# Revit family: WALL WASHER FOCUS RGBW_LVL4030RGB.10
name_source: partatom
category: Luminarias
units: mm (PartAtom-declared; Revit-internal decimal feet)

## family parameters
Compartido = No
Corte con vacíos al cargar = No
Cota de conector redondo = Diámetro de uso
Origen de luz = Sí
Punto de cálculo de habitación = No
Se basa en plano de trabajo = Sí
Siempre vertical = No
Tipo de pieza = Normal

## types (1)
- REFL_LVL4030RGB.10
    Cambio de temperatura de color de luz atenuada = <Ninguno>
    Comentarios de vataje = 90-277V
    Descripción = LUMINARIA TIPO REFLECTOR DIRIGIBLE, WALL WASHER , CUERPO DE ALUMINIO FUNDIDO A PRESION, 279MM DE LARGO POR 162MM DE DIAMETRO CON UN PESO DE 4.2KG, CUENTA CON 4 LED TIPO CREE RGBW CON UN CONSUMO TOTAL DE 45W, 1373 LUMENES, IP 66, CABLE H05RN DE 1.5M, APERTURA DE 10 GRADOS EN STOCK, ALIMENTADA CON FUENTE REMOTA A 90-277V. REQUIERE ACCESORIOS.
    Elevación por defecto = 0 mm  [stored 0 ft]
    Fabricante = BRILLANT
    Filtro de color = 16777215
    Longitud de línea de emisión = 610 mm
    Lámpara = CREE
    Modelo = LVL4030RGB.10
    Tamaño de símbolo de origen de luz = 500 mm
    Watt per fixture = 45

note: [stored X ft] marks values corroborated as IEEE doubles in the binary element streams (Revit-internal decimal feet)

## geometry (parser evidence)
native form markers: Blend x2
no freeform markers — native parametric forms only
